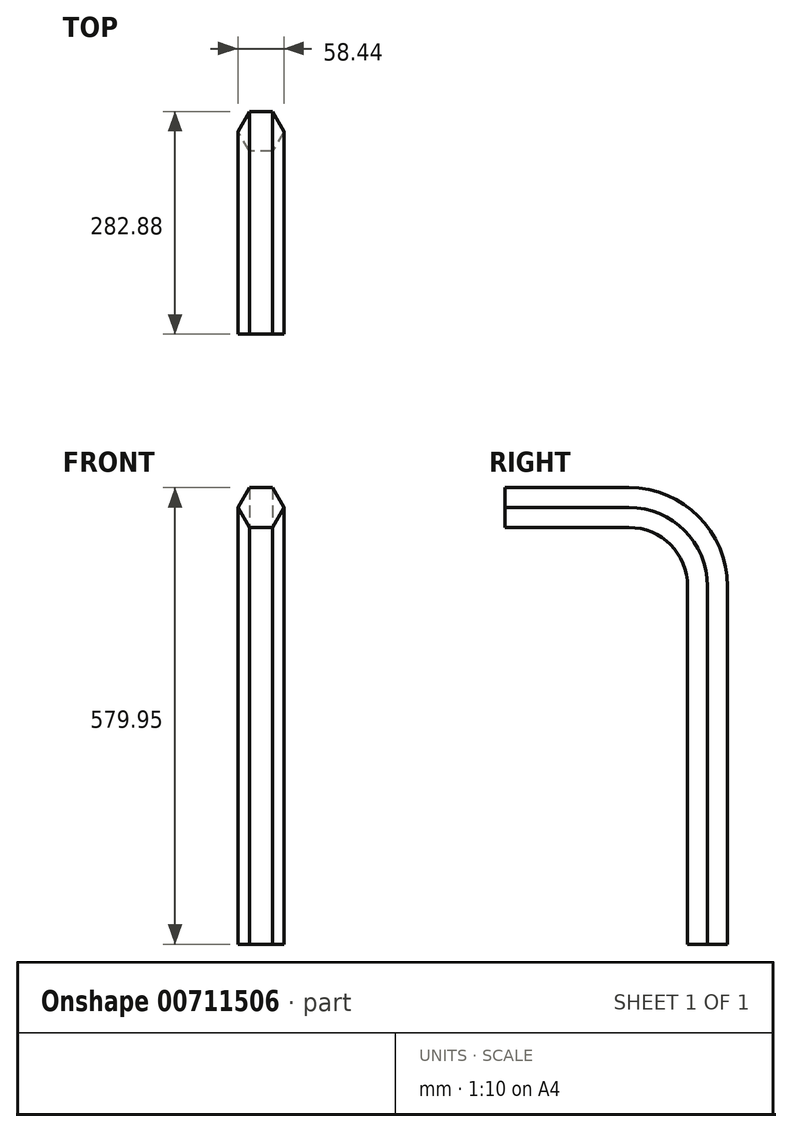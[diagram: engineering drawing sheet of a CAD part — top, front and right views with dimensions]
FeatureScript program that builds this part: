
annotation { "Feature Type Name" : "Feature", "Feature Type Description" : "" }
export const myFeature = defineFeature(function(context is Context, id is Id, definition is map)
    precondition{}
    {
        {
            var Q0;
            Q0=qCreatedBy(makeId("Front.planeOp"),FACE);
            var sketch = newSketch(context, id + "F0", { "sketchPlane" : qUnion([Q0])});
            skCircle(sketch, "E0.cCircle", {"center": v(0, 0) * mm, "radius": 25.3 * mm, "construction": true});
            skLineSegment(sketch, "E0.0", {"start": v(14.61, -25.3) * mm, "end": v(-14.61, -25.3) * mm});
            skLineSegment(sketch, "E0.1", {"start": v(-14.61, -25.3) * mm, "end": v(-29.22, 0) * mm});
            skLineSegment(sketch, "E0.2", {"start": v(-29.22, 0) * mm, "end": v(-14.61, 25.3) * mm});
            skLineSegment(sketch, "E0.3", {"start": v(-14.61, 25.3) * mm, "end": v(14.61, 25.3) * mm});
            skLineSegment(sketch, "E0.4", {"start": v(14.61, 25.3) * mm, "end": v(29.22, 0) * mm});
            skLineSegment(sketch, "E0.5", {"start": v(29.22, 0) * mm, "end": v(14.61, -25.3) * mm});
            skPoint(sketch, "E0.0.midPoint", {"position": v(0, -25.3) * mm});
            skSolve(sketch);
        }
        {
            var Q0;
            Q0=qCreatedBy(makeId("Right.planeOp"),FACE);
            var sketch = newSketch(context, id + "F1", { "sketchPlane" : qUnion([Q0])});
            skLineSegment(sketch, "E1", {"start": v(0, 0) * mm, "end": v(157.58, 0) * mm});
            skLineSegment(sketch, "E2", {"start": v(257.58, -100) * mm, "end": v(257.58, -554.64) * mm});
            skPoint(sketch, "E3.visualSharp", {"position": v(257.58, 0) * mm});
            skArc(sketch, "E3.filletArc", {"start": v(257.58, -100) * mm, "mid": v(228.29, -29.29) * mm, "end": v(157.58, 0) * mm});
            skSolve(sketch);
        }
        {
            var Q0;
            Q0 = qSketchRegion(id + "F0", true);
            var Q1;
            Q1=sQuery(id+"F1.wireOp",EDGE,"E1");
            var Q2;
            Q2=sQuery(id+"F1.wireOp",EDGE,"E3.filletArc");
            var Q3;
            Q3=sQuery(id+"F1.wireOp",EDGE,"E2");
            sweep(context, id + "F2", {"profiles" : qUnion([Q0]), "path" : qUnion([Q1, Q2, Q3])});
        }
    });
